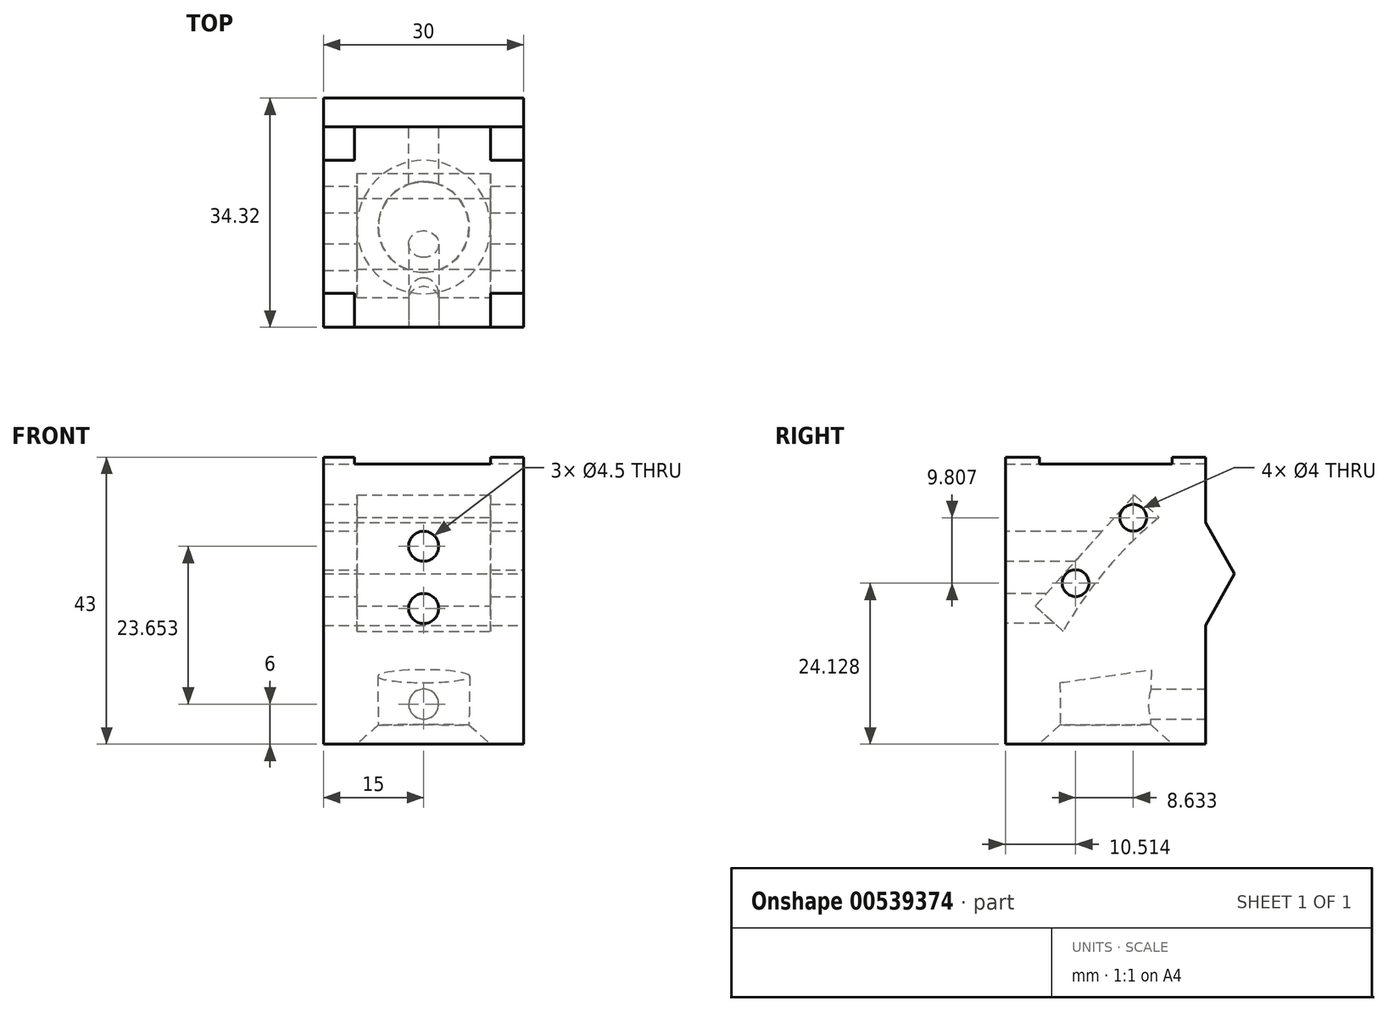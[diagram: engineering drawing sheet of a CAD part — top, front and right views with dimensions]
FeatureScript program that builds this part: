
annotation { "Feature Type Name" : "Feature", "Feature Type Description" : "" }
export const myFeature = defineFeature(function(context is Context, id is Id, definition is map)
    precondition{}
    {
        {
            var Q0;
            Q0=qCreatedBy(makeId("Top.planeOp"),FACE);
            var sketch = newSketch(context, id + "F0", { "sketchPlane" : qUnion([Q0])});
            skLineSegment(sketch, "E0.bottom", {"start": v(-15, 15) * mm, "end": v(15, 15) * mm});
            skLineSegment(sketch, "E0.top", {"start": v(-15, -15) * mm, "end": v(15, -15) * mm});
            skLineSegment(sketch, "E0.left", {"start": v(-15, 15) * mm, "end": v(-15, -15) * mm});
            skLineSegment(sketch, "E0.right", {"start": v(15, 15) * mm, "end": v(15, -15) * mm});
            skSolve(sketch);
        }
        {
            var Q0;
            Q0=qSketchRegion(id+"F0",true);
            extrude(context, id + "F1", {"entities" : qUnion([Q0]), "depth" : 42 * mm, "offsetDistance" : 25 * mm});
        }
        {
            var Q0;
            Q0=qCreatedBy(makeId("Top.planeOp"),FACE);
            var sketch = newSketch(context, id + "F2", { "sketchPlane" : qUnion([Q0])});
            skCircle(sketch, "E1", {"center": v(0, 0) * mm, "radius": 6.75 * mm});
            skSolve(sketch);
        }
        {
            var Q0;
            Q0=qCreatedBy(makeId("Right.planeOp"),FACE);
            var sketch = newSketch(context, id + "F3", { "sketchPlane" : qUnion([Q0])});
            skLineSegment(sketch, "E2", {"start": v(-21.52, 0) * mm, "end": v(19.56, 48.96) * mm});
            skSolve(sketch);
        }
        {
            var Q0;
            Q0=qCreatedBy(makeId("Right.planeOp"),FACE);
            cPlane(context, id + "F4", {"entities" : qUnion([Q0]), "cplaneType" : CPlaneType.OFFSET, "offset" : 15 * mm, "width" : 150 * mm, "height" : 150 * mm});
        }
        {
            var Q0;
            Q0=qCreatedBy(id+"F4.planeOp",FACE);
            var sketch = newSketch(context, id + "F5", { "sketchPlane" : qUnion([Q0])});
            skCircle(sketch, "E3", {"center": v(-4.49, 24.13) * mm, "radius": 2 * mm});
            skCircle(sketch, "E4", {"center": v(4.15, 33.94) * mm, "radius": 2 * mm});
            skSolve(sketch);
        }
        {
            var Q0;
            Q0=qSketchRegion(id+"F5",true);
            extrude(context, id + "F6", {"entities" : qUnion([Q0]), "operationType" : NewBodyOperationType.REMOVE, "oppositeDirection" : true, "depth" : 50 * mm, "offsetDistance" : 25 * mm});
        }
        {
            var Q0;
            Q0=qCreatedBy(makeId("Front.planeOp"),FACE);
            cPlane(context, id + "F7", {"entities" : qUnion([Q0]), "cplaneType" : CPlaneType.OFFSET, "offset" : 15 * mm, "width" : 150 * mm, "height" : 150 * mm});
        }
        {
            var Q0;
            Q0=qCreatedBy(id+"F7.planeOp",FACE);
            var sketch = newSketch(context, id + "F8", { "sketchPlane" : qUnion([Q0])});
            skCircle(sketch, "E5", {"center": v(0, 20.33) * mm, "radius": 2.25 * mm});
            skSolve(sketch);
        }
        {
            var Q0;
            Q0=qSketchRegion(id+"F8",true);
            extrude(context, id + "F9", {"entities" : qUnion([Q0]), "operationType" : NewBodyOperationType.REMOVE, "oppositeDirection" : true, "depth" : 8 * mm, "offsetDistance" : 25 * mm});
        }
        {
            var Q0;
            Q0=qCreatedBy(id+"F7.planeOp",FACE);
            var sketch = newSketch(context, id + "F10", { "sketchPlane" : qUnion([Q0])});
            skCircle(sketch, "E6", {"center": v(0, 29.65) * mm, "radius": 2.25 * mm});
            skSolve(sketch);
        }
        {
            var Q0;
            Q0=qSketchRegion(id+"F10",true);
            extrude(context, id + "F11", {"entities" : qUnion([Q0]), "operationType" : NewBodyOperationType.REMOVE, "oppositeDirection" : true, "depth" : 16 * mm, "offsetDistance" : 25 * mm});
        }
        {
            var Q0;
            Q0=makeQuery(id+"F1.opExtrude","CAP_FACE",FACE,{"disambiguationData":[OSD([sQuery(id+"F0.wireOp",EDGE,"E0.bottom"),sQuery(id+"F0.wireOp",EDGE,"E0.top"),sQuery(id+"F0.wireOp",EDGE,"E0.left"),sQuery(id+"F0.wireOp",EDGE,"E0.right")])],"isStart":false});
            var sketch = newSketch(context, id + "F12", { "sketchPlane" : qUnion([Q0])});
            skLineSegment(sketch, "E7.bottom", {"start": v(15, 15) * mm, "end": v(10, 15) * mm});
            skLineSegment(sketch, "E7.top", {"start": v(15, 10) * mm, "end": v(10, 10) * mm});
            skLineSegment(sketch, "E7.left", {"start": v(15, 15) * mm, "end": v(15, 10) * mm});
            skLineSegment(sketch, "E7.right", {"start": v(10, 15) * mm, "end": v(10, 10) * mm});
            skLineSegment(sketch, "E8.bottom", {"start": v(15, -15) * mm, "end": v(10, -15) * mm});
            skLineSegment(sketch, "E8.top", {"start": v(15, -9.92) * mm, "end": v(10, -9.92) * mm});
            skLineSegment(sketch, "E8.left", {"start": v(15, -15) * mm, "end": v(15, -9.92) * mm});
            skLineSegment(sketch, "E8.right", {"start": v(10, -15) * mm, "end": v(10, -9.92) * mm});
            skLineSegment(sketch, "E9.bottom", {"start": v(-15, -15) * mm, "end": v(-10.38, -15) * mm});
            skLineSegment(sketch, "E9.top", {"start": v(-15, -9.92) * mm, "end": v(-10.38, -9.92) * mm});
            skLineSegment(sketch, "E9.left", {"start": v(-15, -15) * mm, "end": v(-15, -9.92) * mm});
            skLineSegment(sketch, "E9.right", {"start": v(-10.38, -15) * mm, "end": v(-10.38, -9.92) * mm});
            skLineSegment(sketch, "E10.bottom", {"start": v(-15, 15) * mm, "end": v(-10.38, 15) * mm});
            skLineSegment(sketch, "E10.top", {"start": v(-15, 10) * mm, "end": v(-10.38, 10) * mm});
            skLineSegment(sketch, "E10.left", {"start": v(-15, 15) * mm, "end": v(-15, 10) * mm});
            skLineSegment(sketch, "E10.right", {"start": v(-10.38, 15) * mm, "end": v(-10.38, 10) * mm});
            skSolve(sketch);
        }
        {
            var Q0;
            Q0=qSketchRegion(id+"F12",true);
            extrude(context, id + "F13", {"entities" : qUnion([Q0]), "operationType" : NewBodyOperationType.ADD, "depth" : 1 * mm, "offsetDistance" : 25 * mm});
        }
        {
            var Q0;
            Q0=qCreatedBy(makeId("Right.planeOp"),FACE);
            cPlane(context, id + "F14", {"entities" : qUnion([Q0]), "cplaneType" : CPlaneType.OFFSET, "offset" : 10 * mm, "width" : 150 * mm, "height" : 150 * mm});
        }
        {
            var Q0;
            Q0=qCreatedBy(id+"F14.planeOp",FACE);
            var sketch = newSketch(context, id + "F15", { "sketchPlane" : qUnion([Q0])});
            skArc(sketch, "E11", {"start": v(-6.34, 16.93) * mm, "mid": v(0.06, 26.12) * mm, "end": v(8.03, 34) * mm});
            skLineSegment(sketch, "E12", {"start": v(-6.34, 16.93) * mm, "end": v(-10.54, 20.68) * mm});
            skLineSegment(sketch, "E13", {"start": v(-10.54, 20.68) * mm, "end": v(4.3, 37.32) * mm});
            skLineSegment(sketch, "E14", {"start": v(4.3, 37.32) * mm, "end": v(8.03, 34) * mm});
            skSolve(sketch);
        }
        {
            var Q0;
            Q0 = qSketchRegion(id + "F15", true);
            extrude(context, id + "F16", {"entities" : qUnion([Q0]), "operationType" : NewBodyOperationType.REMOVE, "oppositeDirection" : true, "depth" : 20 * mm, "offsetDistance" : 25 * mm});
        }
        {
            var Q0;
            Q0=qCreatedBy(makeId("Front.planeOp"),FACE);
            var sketch = newSketch(context, id + "F17", { "sketchPlane" : qUnion([Q0])});
            skLineSegment(sketch, "E15", {"start": v(0, 9) * mm, "end": v(10, 0) * mm});
            skLineSegment(sketch, "E16", {"start": v(10, 0) * mm, "end": v(0, 0) * mm});
            skLineSegment(sketch, "E17", {"start": v(0, 0) * mm, "end": v(0, 9) * mm});
            skSolve(sketch);
        }
        {
            var Q0;
            Q0 = qSketchRegion(id + "F17", true);
            var Q1;
            Q1=sQuery(id+"F17.wireOp",EDGE,"E17");
            revolve(context, id + "F18", {"operationType" : NewBodyOperationType.REMOVE, "entities" : qUnion([Q0]), "axis" : qUnion([Q1]), "revolveType" : RevolveType.FULL, "oppositeDirection" : true});
        }
        {
            var Q0;
            Q0=makeQuery(id+"F1.opExtrude","CAP_FACE",FACE,{"disambiguationData":[OSD([sQuery(id+"F0.wireOp",EDGE,"E0.bottom"),sQuery(id+"F0.wireOp",EDGE,"E0.top"),sQuery(id+"F0.wireOp",EDGE,"E0.left"),sQuery(id+"F0.wireOp",EDGE,"E0.right")])],"isStart":true});
            var Q1;
            Q1=makeQuery(id+"F1.opExtrude","CAP_EDGE",EDGE,{"disambiguationData":[OSD([sQuery(id+"F0.wireOp",EDGE,"E0.top")])],"isStart":true});
            cPlane(context, id + "F19", {"entities" : qUnion([Q0, Q1]), "cplaneType" : CPlaneType.LINE_ANGLE, "offset" : 25 * mm, "angle" : 8 * degree, "width" : 150 * mm, "height" : 150 * mm});
        }
        {
            var Q0;
            Q0=qCreatedBy(id+"F19.planeOp",FACE);
            cPlane(context, id + "F20", {"entities" : qUnion([Q0]), "cplaneType" : CPlaneType.OFFSET, "offset" : 8 * mm, "width" : 150 * mm, "height" : 150 * mm});
        }
        {
            var Q0;
            Q0=qCreatedBy(id+"F20.planeOp",FACE);
            var sketch = newSketch(context, id + "F21", { "sketchPlane" : qUnion([Q0])});
            skCircle(sketch, "E18", {"center": v(0, 1.42) * mm, "radius": 6.9 * mm});
            skSolve(sketch);
        }
        {
            var Q1;
            Q1 = qSketchRegion(id + "F21", true);
            var Q2;
            Q2 = qSketchRegion(id + "F2", true);
            loft(context, id + "F22", {"operationType" : NewBodyOperationType.REMOVE, "sheetProfilesArray" : [{ "sheetProfileEntities" : qUnion([Q1]) }, { "sheetProfileEntities" : qUnion([Q2]) }]});
        }
        {
            var Q0;
            {var subQ2=sQuery(id+"F0.wireOp",EDGE,"E0.bottom");Q0=makeQuery(id+"FEm8utIFciNoOv7_1.boolean.opBoolean","SPLIT",FACE,{"disambiguationData":[TD([makeQuery(id+"FEm8utIFciNoOv7_1.opExtrude","SWEPT_FACE",FACE,{"disambiguationData":[OSD([sQuery(id+"FVPy0T7svAIJRco_1.wireOp",EDGE,"Tx6TCgtF-upVV-gQSA-nJ1N-y7oTboYNP6Ox.top")])]})])],"derivedFrom":makeQuery(id+"F13.boolean.opBoolean","MERGE",FACE,{"derivedFrom":[makeQuery(id+"F1.opExtrude","SWEPT_FACE",FACE,{"disambiguationData":[OSD([subQ2])]}),makeQuery(id+"F13.opExtrude","SWEPT_FACE",FACE,{"disambiguationData":[OSD([sQuery(id+"F12.wireOp",EDGE,"E7.bottom")])]}),makeQuery(id+"F13.opExtrude","SWEPT_FACE",FACE,{"disambiguationData":[OSD([sQuery(id+"F12.wireOp",EDGE,"E10.bottom")])]})]})});}
            var sketch = newSketch(context, id + "F23", { "sketchPlane" : qUnion([Q0])});
            skCircle(sketch, "E19", {"center": v(0, 6) * mm, "radius": 2.25 * mm});
            skSolve(sketch);
        }
        {
            var Q0;
            Q0 = qSketchRegion(id + "F23", true);
            extrude(context, id + "F24", {"entities" : qUnion([Q0]), "operationType" : NewBodyOperationType.REMOVE, "endBound" : BoundingType.UP_TO_NEXT, "oppositeDirection" : true, "depth" : 25 * mm, "offsetDistance" : 25 * mm});
        }
        {
            var Q0;
            Q0=makeQuery(id+"F13.boolean.opBoolean","MERGE",FACE,{"derivedFrom":[makeQuery(id+"F1.opExtrude","SWEPT_FACE",FACE,{"disambiguationData":[OSD([sQuery(id+"F0.wireOp",EDGE,"E0.right")])]}),makeQuery(id+"F13.opExtrude","SWEPT_FACE",FACE,{"disambiguationData":[OSD([sQuery(id+"F12.wireOp",EDGE,"E7.left")])]}),makeQuery(id+"F13.opExtrude","SWEPT_FACE",FACE,{"disambiguationData":[OSD([sQuery(id+"F12.wireOp",EDGE,"E8.left")])]})]});
            var sketch = newSketch(context, id + "F25", { "sketchPlane" : qUnion([Q0])});
            skLineSegment(sketch, "E20", {"start": v(15, 33.23) * mm, "end": v(19.32, 25.52) * mm});
            skLineSegment(sketch, "E21", {"start": v(19.32, 25.52) * mm, "end": v(15, 17.81) * mm});
            skSolve(sketch);
        }
        {
            var Q0;
            {var subQ0=sQuery(id+"F25.wireOp",EDGE,"E20");Q0=makeQuery(id+"F25.imprint","IMPRINT",FACE,{"disambiguationData":[TD([[makeQuery(id+"F25.imprint","IMPRINT",EDGE,{"derivedFrom":subQ0}),-1.0]])]});}
            extrude(context, id + "F26", {"entities" : qUnion([Q0]), "operationType" : NewBodyOperationType.ADD, "oppositeDirection" : true, "depth" : 30 * mm, "offsetDistance" : 25 * mm});
        }
    });
